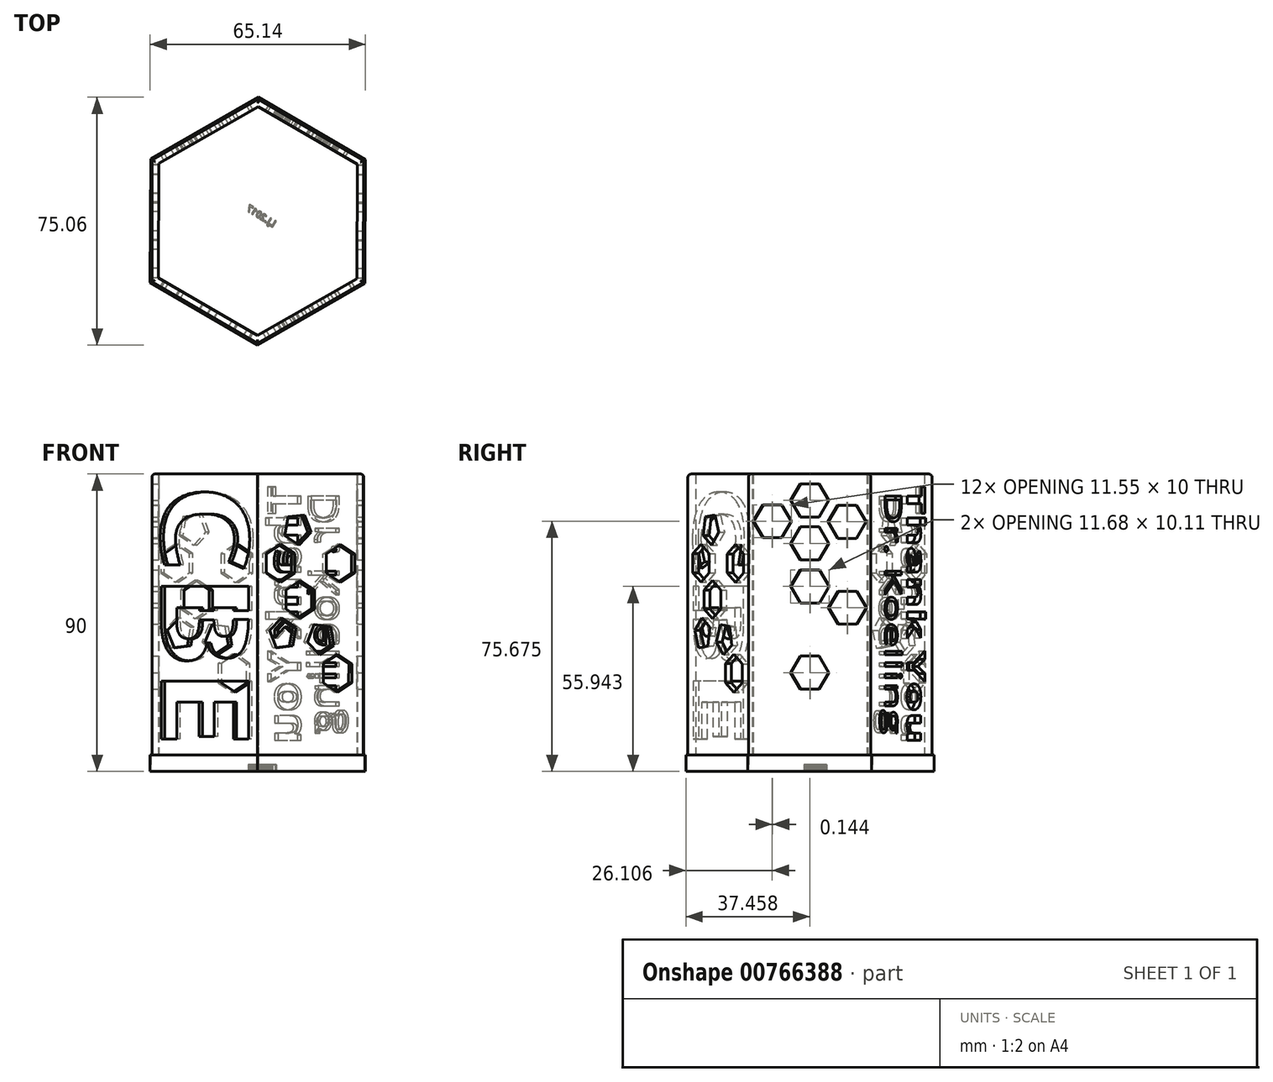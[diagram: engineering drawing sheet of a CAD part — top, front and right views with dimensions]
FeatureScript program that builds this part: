
annotation { "Feature Type Name" : "Feature", "Feature Type Description" : "" }
export const myFeature = defineFeature(function(context is Context, id is Id, definition is map)
    precondition{}
    {
        {
            var Q0;
            Q0=qCreatedBy(makeId("Top.planeOp"),FACE);
            var sketch = newSketch(context, id + "F0", { "sketchPlane" : qUnion([Q0])});
            skCircle(sketch, "E0.cCircle", {"center": v(0, 0) * mm, "radius": 32 * mm, "construction": true});
            skLineSegment(sketch, "E0.0", {"start": v(-31.96, 18.55) * mm, "end": v(0.09, 36.95) * mm});
            skLineSegment(sketch, "E0.1", {"start": v(0.09, 36.95) * mm, "end": v(32.04, 18.4) * mm});
            skLineSegment(sketch, "E0.2", {"start": v(32.04, 18.4) * mm, "end": v(31.96, -18.55) * mm});
            skLineSegment(sketch, "E0.3", {"start": v(31.96, -18.55) * mm, "end": v(-0.09, -36.95) * mm});
            skLineSegment(sketch, "E0.4", {"start": v(-0.09, -36.95) * mm, "end": v(-32.04, -18.4) * mm});
            skLineSegment(sketch, "E0.5", {"start": v(-32.04, -18.4) * mm, "end": v(-31.96, 18.55) * mm});
            skPoint(sketch, "E0.0.midPoint", {"position": v(-15.93, 27.75) * mm});
            skCircle(sketch, "E1.cCircle", {"center": v(0, 0) * mm, "radius": 30 * mm, "construction": true});
            skLineSegment(sketch, "E1.0", {"start": v(-29.93, 17.44) * mm, "end": v(0.13, 34.64) * mm});
            skLineSegment(sketch, "E1.1", {"start": v(0.13, 34.64) * mm, "end": v(30.07, 17.2) * mm});
            skLineSegment(sketch, "E1.2", {"start": v(30.07, 17.2) * mm, "end": v(29.93, -17.44) * mm});
            skLineSegment(sketch, "E1.3", {"start": v(29.93, -17.44) * mm, "end": v(-0.13, -34.64) * mm});
            skLineSegment(sketch, "E1.4", {"start": v(-0.13, -34.64) * mm, "end": v(-30.07, -17.2) * mm});
            skLineSegment(sketch, "E1.5", {"start": v(-30.07, -17.2) * mm, "end": v(-29.93, 17.44) * mm});
            skPoint(sketch, "E1.0.midPoint", {"position": v(-14.9, 26.04) * mm});
            skSolve(sketch);
        }
        {
            var Q0;
            Q0=makeQuery(id+"F0.imprint","IMPRINT",FACE,{"disambiguationData":[TD([[makeQuery(id+"F0.imprint","IMPRINT",EDGE,{"derivedFrom":sQuery(id+"F0.wireOp",EDGE,"E0.0")}),-1.0]])]});
            extrude(context, id + "F1", {"entities" : qUnion([Q0]), "depth" : 90 * mm, "offsetDistance" : 25 * mm});
        }
        {
            var Q0;
            Q0=qCreatedBy(makeId("Top.planeOp"),FACE);
            var sketch = newSketch(context, id + "F2", { "sketchPlane" : qUnion([Q0])});
            skCircle(sketch, "E2.cCircle", {"center": v(0, 0) * mm, "radius": 32.5 * mm, "construction": true});
            skLineSegment(sketch, "E2.0", {"start": v(0.14, 37.53) * mm, "end": v(32.57, 18.64) * mm});
            skLineSegment(sketch, "E2.1", {"start": v(32.57, 18.64) * mm, "end": v(32.43, -18.89) * mm});
            skLineSegment(sketch, "E2.2", {"start": v(32.43, -18.89) * mm, "end": v(-0.14, -37.53) * mm});
            skLineSegment(sketch, "E2.3", {"start": v(-0.14, -37.53) * mm, "end": v(-32.57, -18.64) * mm});
            skLineSegment(sketch, "E2.4", {"start": v(-32.57, -18.64) * mm, "end": v(-32.43, 18.89) * mm});
            skLineSegment(sketch, "E2.5", {"start": v(-32.43, 18.89) * mm, "end": v(0.14, 37.53) * mm});
            skPoint(sketch, "E2.0.midPoint", {"position": v(16.36, 28.08) * mm});
            skSolve(sketch);
        }
        {
            var Q0;
            Q0=makeQuery(id+"F2.imprint","IMPRINT",FACE,{"disambiguationData":[TD([[makeQuery(id+"F2.imprint","IMPRINT",EDGE,{"derivedFrom":sQuery(id+"F2.wireOp",EDGE,"E2.0")}),-1.0]])]});
            extrude(context, id + "F3", {"entities" : qUnion([Q0]), "operationType" : NewBodyOperationType.ADD, "depth" : 5 * mm, "offsetDistance" : 25 * mm});
        }
        {
            var Q0;
            Q0=makeQuery(id+"F1.opExtrude","SWEPT_FACE",FACE,{"disambiguationData":[OSD([sQuery(id+"F0.wireOp",EDGE,"E0.2")])]});
            var sketch = newSketch(context, id + "F4", { "sketchPlane" : qUnion([Q0])});
            skCircle(sketch, "E3.cCircle", {"center": v(0, 82) * mm, "radius": 5 * mm, "construction": true});
            skLineSegment(sketch, "E3.0", {"start": v(-2.89, 87) * mm, "end": v(2.89, 87) * mm});
            skLineSegment(sketch, "E3.1", {"start": v(2.89, 87) * mm, "end": v(5.77, 82) * mm});
            skLineSegment(sketch, "E3.2", {"start": v(5.77, 82) * mm, "end": v(2.89, 77) * mm});
            skLineSegment(sketch, "E3.3", {"start": v(2.89, 77) * mm, "end": v(-2.89, 77) * mm});
            skLineSegment(sketch, "E3.4", {"start": v(-2.89, 77) * mm, "end": v(-5.77, 82) * mm});
            skLineSegment(sketch, "E3.5", {"start": v(-5.77, 82) * mm, "end": v(-2.89, 87) * mm});
            skPoint(sketch, "E3.0.midPoint", {"position": v(0, 87) * mm});
            skCircle(sketch, "E4.cCircle", {"center": v(-11.35, 75.68) * mm, "radius": 5 * mm, "construction": true});
            skLineSegment(sketch, "E4.0", {"start": v(-14.24, 80.68) * mm, "end": v(-8.47, 80.68) * mm});
            skLineSegment(sketch, "E4.1", {"start": v(-8.47, 80.68) * mm, "end": v(-5.58, 75.68) * mm});
            skLineSegment(sketch, "E4.2", {"start": v(-5.58, 75.68) * mm, "end": v(-8.47, 70.68) * mm});
            skLineSegment(sketch, "E4.3", {"start": v(-8.47, 70.68) * mm, "end": v(-14.24, 70.68) * mm});
            skLineSegment(sketch, "E4.4", {"start": v(-14.24, 70.68) * mm, "end": v(-17.13, 75.68) * mm});
            skLineSegment(sketch, "E4.5", {"start": v(-17.13, 75.68) * mm, "end": v(-14.24, 80.68) * mm});
            skPoint(sketch, "E4.0.midPoint", {"position": v(-11.35, 80.68) * mm});
            skCircle(sketch, "E5.cCircle", {"center": v(11.26, 75.5) * mm, "radius": 5 * mm, "construction": true});
            skLineSegment(sketch, "E5.0", {"start": v(8.37, 80.5) * mm, "end": v(14.15, 80.5) * mm});
            skLineSegment(sketch, "E5.1", {"start": v(14.15, 80.5) * mm, "end": v(17.03, 75.5) * mm});
            skLineSegment(sketch, "E5.2", {"start": v(17.03, 75.5) * mm, "end": v(14.15, 70.5) * mm});
            skLineSegment(sketch, "E5.3", {"start": v(14.15, 70.5) * mm, "end": v(8.37, 70.5) * mm});
            skLineSegment(sketch, "E5.4", {"start": v(8.37, 70.5) * mm, "end": v(5.48, 75.5) * mm});
            skLineSegment(sketch, "E5.5", {"start": v(5.48, 75.5) * mm, "end": v(8.37, 80.5) * mm});
            skPoint(sketch, "E5.0.midPoint", {"position": v(11.26, 80.5) * mm});
            skCircle(sketch, "E6.cCircle", {"center": v(0, 69) * mm, "radius": 5 * mm, "construction": true});
            skLineSegment(sketch, "E6.0", {"start": v(-2.89, 74) * mm, "end": v(2.89, 74) * mm});
            skLineSegment(sketch, "E6.1", {"start": v(2.89, 74) * mm, "end": v(5.77, 69) * mm});
            skLineSegment(sketch, "E6.2", {"start": v(5.77, 69) * mm, "end": v(2.89, 64) * mm});
            skLineSegment(sketch, "E6.3", {"start": v(2.89, 64) * mm, "end": v(-2.89, 64) * mm});
            skLineSegment(sketch, "E6.4", {"start": v(-2.89, 64) * mm, "end": v(-5.77, 69) * mm});
            skLineSegment(sketch, "E6.5", {"start": v(-5.77, 69) * mm, "end": v(-2.89, 74) * mm});
            skPoint(sketch, "E6.0.midPoint", {"position": v(0, 74) * mm});
            skCircle(sketch, "E7.cCircle", {"center": v(0, 55.94) * mm, "radius": 5.06 * mm, "construction": true});
            skLineSegment(sketch, "E7.0", {"start": v(-5.84, 55.94) * mm, "end": v(-2.92, 61) * mm});
            skLineSegment(sketch, "E7.1", {"start": v(-2.92, 61) * mm, "end": v(2.92, 61) * mm});
            skLineSegment(sketch, "E7.2", {"start": v(2.92, 61) * mm, "end": v(5.84, 55.94) * mm});
            skLineSegment(sketch, "E7.3", {"start": v(5.84, 55.94) * mm, "end": v(2.92, 50.89) * mm});
            skLineSegment(sketch, "E7.4", {"start": v(2.92, 50.89) * mm, "end": v(-2.92, 50.89) * mm});
            skLineSegment(sketch, "E7.5", {"start": v(-2.92, 50.89) * mm, "end": v(-5.84, 55.94) * mm});
            skPoint(sketch, "E7.0.midPoint", {"position": v(-4.38, 58.47) * mm});
            skCircle(sketch, "E8.cCircle", {"center": v(11.37, 49.53) * mm, "radius": 5 * mm, "construction": true});
            skLineSegment(sketch, "E8.0", {"start": v(5.6, 49.53) * mm, "end": v(8.49, 54.53) * mm});
            skLineSegment(sketch, "E8.1", {"start": v(8.49, 54.53) * mm, "end": v(14.26, 54.53) * mm});
            skLineSegment(sketch, "E8.2", {"start": v(14.26, 54.53) * mm, "end": v(17.15, 49.53) * mm});
            skLineSegment(sketch, "E8.3", {"start": v(17.15, 49.53) * mm, "end": v(14.26, 44.53) * mm});
            skLineSegment(sketch, "E8.4", {"start": v(14.26, 44.53) * mm, "end": v(8.49, 44.53) * mm});
            skLineSegment(sketch, "E8.5", {"start": v(8.49, 44.53) * mm, "end": v(5.6, 49.53) * mm});
            skPoint(sketch, "E8.0.midPoint", {"position": v(7.04, 52.03) * mm});
            skCircle(sketch, "E9.cCircle", {"center": v(0, 29.89) * mm, "radius": 5 * mm, "construction": true});
            skLineSegment(sketch, "E9.0", {"start": v(-5.77, 29.89) * mm, "end": v(-2.89, 34.89) * mm});
            skLineSegment(sketch, "E9.1", {"start": v(-2.89, 34.89) * mm, "end": v(2.89, 34.89) * mm});
            skLineSegment(sketch, "E9.2", {"start": v(2.89, 34.89) * mm, "end": v(5.77, 29.89) * mm});
            skLineSegment(sketch, "E9.3", {"start": v(5.77, 29.89) * mm, "end": v(2.89, 24.89) * mm});
            skLineSegment(sketch, "E9.4", {"start": v(2.89, 24.89) * mm, "end": v(-2.89, 24.89) * mm});
            skLineSegment(sketch, "E9.5", {"start": v(-2.89, 24.89) * mm, "end": v(-5.77, 29.89) * mm});
            skPoint(sketch, "E9.0.midPoint", {"position": v(-4.33, 32.39) * mm});
            skSolve(sketch);
        }
        {
            var Q0;
            Q0=makeQuery(id+"F4.imprint","IMPRINT",FACE,{"disambiguationData":[TD([[makeQuery(id+"F4.imprint","IMPRINT",EDGE,{"derivedFrom":sQuery(id+"F4.wireOp",EDGE,"E3.0")}),-1.0]])]});
            var Q1;
            Q1=makeQuery(id+"F4.imprint","IMPRINT",FACE,{"disambiguationData":[TD([[makeQuery(id+"F4.imprint","IMPRINT",EDGE,{"derivedFrom":sQuery(id+"F4.wireOp",EDGE,"E5.0")}),-1.0]])]});
            var Q2;
            Q2=makeQuery(id+"F4.imprint","IMPRINT",FACE,{"disambiguationData":[TD([[makeQuery(id+"F4.imprint","IMPRINT",EDGE,{"derivedFrom":sQuery(id+"F4.wireOp",EDGE,"E4.0")}),-1.0]])]});
            var Q3;
            Q3=makeQuery(id+"F4.imprint","IMPRINT",FACE,{"disambiguationData":[TD([[makeQuery(id+"F4.imprint","IMPRINT",EDGE,{"derivedFrom":sQuery(id+"F4.wireOp",EDGE,"E6.0")}),-1.0]])]});
            var Q4;
            Q4=makeQuery(id+"F4.imprint","IMPRINT",FACE,{"disambiguationData":[TD([[makeQuery(id+"F4.imprint","IMPRINT",EDGE,{"derivedFrom":sQuery(id+"F4.wireOp",EDGE,"E7.0")}),-1.0]])]});
            var Q5;
            Q5=makeQuery(id+"F4.imprint","IMPRINT",FACE,{"disambiguationData":[TD([[makeQuery(id+"F4.imprint","IMPRINT",EDGE,{"derivedFrom":sQuery(id+"F4.wireOp",EDGE,"E8.0")}),-1.0]])]});
            var Q6;
            Q6=makeQuery(id+"F4.imprint","IMPRINT",FACE,{"disambiguationData":[TD([[makeQuery(id+"F4.imprint","IMPRINT",EDGE,{"derivedFrom":sQuery(id+"F4.wireOp",EDGE,"E9.0")}),-1.0]])]});
            extrude(context, id + "F5", {"entities" : qUnion([Q0, Q1, Q2, Q3, Q4, Q5, Q6]), "operationType" : NewBodyOperationType.REMOVE, "oppositeDirection" : true, "depth" : 100 * mm, "offsetDistance" : 25 * mm});
        }
        {
            var Q0;
            Q0=makeQuery(id+"F1.opExtrude","CAP_EDGE",EDGE,{"disambiguationData":[OSD([sQuery(id+"F0.wireOp",EDGE,"E0.0")])],"isStart":false});
            var Q1;
            Q1=makeQuery(id+"F1.opExtrude","CAP_EDGE",EDGE,{"disambiguationData":[OSD([sQuery(id+"F0.wireOp",EDGE,"E0.5")])],"isStart":false});
            var Q2;
            Q2=makeQuery(id+"F1.opExtrude","CAP_EDGE",EDGE,{"disambiguationData":[OSD([sQuery(id+"F0.wireOp",EDGE,"E0.2")])],"isStart":false});
            var Q3;
            Q3=makeQuery(id+"F1.opExtrude","CAP_EDGE",EDGE,{"disambiguationData":[OSD([sQuery(id+"F0.wireOp",EDGE,"E0.3")])],"isStart":false});
            var Q4;
            Q4=makeQuery(id+"F1.opExtrude","CAP_EDGE",EDGE,{"disambiguationData":[OSD([sQuery(id+"F0.wireOp",EDGE,"E0.4")])],"isStart":false});
            var Q5;
            Q5=makeQuery(id+"F1.opExtrude","CAP_EDGE",EDGE,{"disambiguationData":[OSD([sQuery(id+"F0.wireOp",EDGE,"E0.1")])],"isStart":false});
            fillet(context, id + "F6", {"entities" : qUnion([Q0, Q1, Q2, Q3, Q4, Q5]), "radius" : 1 * mm, "tangentPropagation" : true, "allowEdgeOverflow" : false});
        }
        {
            var Q0;
            Q0=makeQuery(id+"F1.opExtrude","SWEPT_FACE",FACE,{"disambiguationData":[OSD([sQuery(id+"F0.wireOp",EDGE,"E0.0")])]});
            var sketch = newSketch(context, id + "F7", { "sketchPlane" : qUnion([Q0])});
            skCircle(sketch, "E10.cCircle", {"center": v(-10.48, 62.93) * mm, "radius": 5 * mm, "construction": true});
            skLineSegment(sketch, "E10.0", {"start": v(-15.48, 65.82) * mm, "end": v(-10.48, 68.7) * mm});
            skLineSegment(sketch, "E10.1", {"start": v(-10.48, 68.7) * mm, "end": v(-5.48, 65.82) * mm});
            skLineSegment(sketch, "E10.2", {"start": v(-5.48, 65.82) * mm, "end": v(-5.48, 60.04) * mm});
            skLineSegment(sketch, "E10.3", {"start": v(-5.48, 60.04) * mm, "end": v(-10.48, 57.16) * mm});
            skLineSegment(sketch, "E10.4", {"start": v(-10.48, 57.16) * mm, "end": v(-15.48, 60.04) * mm});
            skLineSegment(sketch, "E10.5", {"start": v(-15.48, 60.04) * mm, "end": v(-15.48, 65.82) * mm});
            skPoint(sketch, "E10.0.midPoint", {"position": v(-12.98, 67.26) * mm});
            skCircle(sketch, "E11.cCircle", {"center": v(10.48, 62.98) * mm, "radius": 5 * mm, "construction": true});
            skLineSegment(sketch, "E11.0", {"start": v(5.48, 65.87) * mm, "end": v(10.48, 68.75) * mm});
            skLineSegment(sketch, "E11.1", {"start": v(10.48, 68.75) * mm, "end": v(15.48, 65.87) * mm});
            skLineSegment(sketch, "E11.2", {"start": v(15.48, 65.87) * mm, "end": v(15.48, 60.1) * mm});
            skLineSegment(sketch, "E11.3", {"start": v(15.48, 60.1) * mm, "end": v(10.48, 57.2) * mm});
            skLineSegment(sketch, "E11.4", {"start": v(10.48, 57.2) * mm, "end": v(5.48, 60.1) * mm});
            skLineSegment(sketch, "E11.5", {"start": v(5.48, 60.1) * mm, "end": v(5.48, 65.87) * mm});
            skPoint(sketch, "E11.0.midPoint", {"position": v(7.98, 67.3) * mm});
            skCircle(sketch, "E12.cCircle", {"center": v(3.52, 51.98) * mm, "radius": 5 * mm, "construction": true});
            skLineSegment(sketch, "E12.0", {"start": v(-1.48, 54.87) * mm, "end": v(3.52, 57.75) * mm});
            skLineSegment(sketch, "E12.1", {"start": v(3.52, 57.75) * mm, "end": v(8.52, 54.87) * mm});
            skLineSegment(sketch, "E12.2", {"start": v(8.52, 54.87) * mm, "end": v(8.52, 49.1) * mm});
            skLineSegment(sketch, "E12.3", {"start": v(8.52, 49.1) * mm, "end": v(3.52, 46.2) * mm});
            skLineSegment(sketch, "E12.4", {"start": v(3.52, 46.2) * mm, "end": v(-1.48, 49.1) * mm});
            skLineSegment(sketch, "E12.5", {"start": v(-1.48, 49.1) * mm, "end": v(-1.48, 54.87) * mm});
            skPoint(sketch, "E12.0.midPoint", {"position": v(1.02, 56.31) * mm});
            skCircle(sketch, "E13.cCircle", {"center": v(-9.5, 29.7) * mm, "radius": 5 * mm, "construction": true});
            skLineSegment(sketch, "E13.0", {"start": v(-14.5, 32.56) * mm, "end": v(-9.52, 35.47) * mm});
            skLineSegment(sketch, "E13.1", {"start": v(-9.52, 35.47) * mm, "end": v(-4.5, 32.61) * mm});
            skLineSegment(sketch, "E13.2", {"start": v(-4.5, 32.61) * mm, "end": v(-4.48, 26.84) * mm});
            skLineSegment(sketch, "E13.3", {"start": v(-4.48, 26.84) * mm, "end": v(-9.46, 23.92) * mm});
            skLineSegment(sketch, "E13.4", {"start": v(-9.46, 23.92) * mm, "end": v(-14.48, 26.79) * mm});
            skLineSegment(sketch, "E13.5", {"start": v(-14.48, 26.79) * mm, "end": v(-14.5, 32.56) * mm});
            skPoint(sketch, "E13.0.midPoint", {"position": v(-12.01, 34.01) * mm});
            skCircle(sketch, "E14.cCircle", {"center": v(9.5, 41.6) * mm, "radius": 3.97 * mm, "construction": true});
            skLineSegment(sketch, "E14.0", {"start": v(10.02, 46.5) * mm, "end": v(14.3, 42.63) * mm});
            skLineSegment(sketch, "E14.1", {"start": v(14.3, 42.63) * mm, "end": v(11.96, 37.36) * mm});
            skLineSegment(sketch, "E14.2", {"start": v(11.96, 37.36) * mm, "end": v(6.22, 37.96) * mm});
            skLineSegment(sketch, "E14.3", {"start": v(6.22, 37.96) * mm, "end": v(5.02, 43.6) * mm});
            skLineSegment(sketch, "E14.4", {"start": v(5.02, 43.6) * mm, "end": v(10.02, 46.5) * mm});
            skPoint(sketch, "E14.0.midPoint", {"position": v(12.16, 44.56) * mm});
            skCircle(sketch, "E15.cCircle", {"center": v(-3.67, 40.16) * mm, "radius": 3.97 * mm, "construction": true});
            skLineSegment(sketch, "E15.0", {"start": v(1.14, 39.16) * mm, "end": v(-3.13, 35.28) * mm});
            skLineSegment(sketch, "E15.1", {"start": v(-3.13, 35.28) * mm, "end": v(-8.14, 38.14) * mm});
            skLineSegment(sketch, "E15.2", {"start": v(-8.14, 38.14) * mm, "end": v(-6.97, 43.8) * mm});
            skLineSegment(sketch, "E15.3", {"start": v(-6.97, 43.8) * mm, "end": v(-1.24, 44.43) * mm});
            skLineSegment(sketch, "E15.4", {"start": v(-1.24, 44.43) * mm, "end": v(1.14, 39.16) * mm});
            skPoint(sketch, "E15.0.midPoint", {"position": v(-1, 37.22) * mm});
            skCircle(sketch, "E16.cCircle", {"center": v(4.52, 73.36) * mm, "radius": 3.97 * mm, "construction": true});
            skLineSegment(sketch, "E16.0", {"start": v(-0.29, 72.34) * mm, "end": v(2.06, 77.62) * mm});
            skLineSegment(sketch, "E16.1", {"start": v(2.06, 77.62) * mm, "end": v(7.8, 77.01) * mm});
            skLineSegment(sketch, "E16.2", {"start": v(7.8, 77.01) * mm, "end": v(9, 71.37) * mm});
            skLineSegment(sketch, "E16.3", {"start": v(9, 71.37) * mm, "end": v(4, 68.48) * mm});
            skLineSegment(sketch, "E16.4", {"start": v(4, 68.48) * mm, "end": v(-0.29, 72.34) * mm});
            skPoint(sketch, "E16.0.midPoint", {"position": v(0.89, 74.98) * mm});
            skSolve(sketch);
        }
        {
            var Q0;
            Q0 = qSketchRegion(id + "F7", true);
            extrude(context, id + "F8", {"entities" : qUnion([Q0]), "operationType" : NewBodyOperationType.REMOVE, "oppositeDirection" : true, "depth" : 100 * mm, "offsetDistance" : 25 * mm});
        }
        {
            var Q0;
            Q0=makeQuery(id+"F1.opExtrude","SWEPT_FACE",FACE,{"disambiguationData":[OSD([sQuery(id+"F0.wireOp",EDGE,"E0.4")])]});
            var sketch = newSketch(context, id + "F9", { "sketchPlane" : qUnion([Q0])});
            skText(sketch, "E17", { "text": "CBE", "fontName": "OpenSans-Bold.ttf"});
            skLineSegment(sketch, "E18", {"start": v(9.93, 48.67) * mm, "end": v(15.57, 48.67) * mm});
            skLineSegment(sketch, "E19", {"start": v(9.93, 45.9) * mm, "end": v(15.57, 45.9) * mm});
            skLineSegment(sketch, "E20", {"start": v(-15.15, 48.67) * mm, "end": v(-9.77, 48.67) * mm});
            skLineSegment(sketch, "E21", {"start": v(-15.15, 45.9) * mm, "end": v(-9.77, 45.9) * mm});
            skLineSegment(sketch, "E22", {"start": v(-1.88, 48.67) * mm, "end": v(3.3, 48.67) * mm});
            skLineSegment(sketch, "E23", {"start": v(3.3, 45.8) * mm, "end": v(-1.88, 45.8) * mm});
            const initialGuessF9  = {"E17": [-0.01515, 0.08703, 0, -1, 0.03072]};
            skSetInitialGuess(sketch, initialGuessF9);
            skSolve(sketch);
        }
        {
            var Q0;
            Q0=makeQuery(id+"F9.imprint","IMPRINT",FACE,{"disambiguationData":[TD([[makeQuery(id+"F9.imprint","IMPRINT",EDGE,{"derivedFrom":sQuery(id+"F9.wireOp",EDGE,"E17.sketch_text.stroke-0")}),-1.0]])]});
            var Q1;
            {var subQ6=sQuery(id+"F9.wireOp",EDGE,"E17.sketch_text.stroke-26");Q1=makeQuery(id+"F9.imprint","IMPRINT",FACE,{"disambiguationData":[TD([[makeQuery(id+"F9.imprint","IMPRINT",EDGE,{"derivedFrom":subQ6}),-1.0]])]});}
            var Q2;
            {var subQ15=sQuery(id+"F9.wireOp",EDGE,"E17.sketch_text.stroke-17");Q2=makeQuery(id+"F9.imprint","IMPRINT",FACE,{"disambiguationData":[TD([[makeQuery(id+"F9.imprint","IMPRINT",EDGE,{"derivedFrom":subQ15}),-1.0]])]});}
            var Q3;
            Q3=makeQuery(id+"F9.imprint","IMPRINT",FACE,{"disambiguationData":[TD([[makeQuery(id+"F9.imprint","IMPRINT",EDGE,{"derivedFrom":sQuery(id+"F9.wireOp",EDGE,"E17.sketch_text.stroke-40")}),-1.0]])]});
            extrude(context, id + "F10", {"entities" : qUnion([Q0, Q1, Q2, Q3]), "operationType" : NewBodyOperationType.REMOVE, "oppositeDirection" : true, "depth" : 30 * mm, "offsetDistance" : 25 * mm});
        }
        {
            var Q0;
            Q0=makeQuery(id+"F1.opExtrude","SWEPT_FACE",FACE,{"disambiguationData":[OSD([sQuery(id+"F0.wireOp",EDGE,"E0.1")])]});
            var sketch = newSketch(context, id + "F11", { "sketchPlane" : qUnion([Q0])});
            skText(sketch, "E24", { "text": "Thank You", "fontName": "OpenSans-Bold.ttf"});
            const initialGuessF11  = {"E24": [0.00347, 0.08644, 0, -1, 0.01067]};
            skSetInitialGuess(sketch, initialGuessF11);
            skSolve(sketch);
        }
        {
            var Q0;
            Q0=makeQuery(id+"F11.imprint","IMPRINT",FACE,{"disambiguationData":[TD([[makeQuery(id+"F11.imprint","IMPRINT",EDGE,{"derivedFrom":sQuery(id+"F11.wireOp",EDGE,"E24.sketch_text.stroke-0")}),1.0]])]});
            var sketch = newSketch(context, id + "F12", { "sketchPlane" : qUnion([Q0])});
            skText(sketch, "E25", { "text": "Dr. Koelling", "fontName": "OpenSans-Regular.ttf"});
            const initialGuessF12  = {"E25": [-0.00986, 0.08466, 0, -1, 0.00986]};
            skSetInitialGuess(sketch, initialGuessF12);
            skSolve(sketch);
        }
        {
            var Q0;
            Q0 = qSketchRegion(id + "F11", true);
            var Q1;
            Q1 = qSketchRegion(id + "F12", true);
            extrude(context, id + "F13", {"entities" : qUnion([Q0, Q1]), "operationType" : NewBodyOperationType.REMOVE, "oppositeDirection" : true, "depth" : 25 * mm, "offsetDistance" : 25 * mm});
        }
        {
            var Q0;
            Q0=makeQuery(id+"F3.boolean.opBoolean","MERGE",FACE,{"derivedFrom":[makeQuery(id+"F1.opExtrude","CAP_FACE",FACE,{"disambiguationData":[OSD([sQuery(id+"F0.wireOp",EDGE,"E0.0"),sQuery(id+"F0.wireOp",EDGE,"E0.1"),sQuery(id+"F0.wireOp",EDGE,"E0.2"),sQuery(id+"F0.wireOp",EDGE,"E0.3"),sQuery(id+"F0.wireOp",EDGE,"E0.4"),sQuery(id+"F0.wireOp",EDGE,"E0.5"),sQuery(id+"F0.wireOp",EDGE,"E1.0"),sQuery(id+"F0.wireOp",EDGE,"E1.1"),sQuery(id+"F0.wireOp",EDGE,"E1.2"),sQuery(id+"F0.wireOp",EDGE,"E1.3"),sQuery(id+"F0.wireOp",EDGE,"E1.4"),sQuery(id+"F0.wireOp",EDGE,"E1.5")])],"isStart":true}),makeQuery(id+"F3.opExtrude","CAP_FACE",FACE,{"disambiguationData":[OSD([sQuery(id+"F2.wireOp",EDGE,"E2.0"),sQuery(id+"F2.wireOp",EDGE,"E2.1"),sQuery(id+"F2.wireOp",EDGE,"E2.2"),sQuery(id+"F2.wireOp",EDGE,"E2.3"),sQuery(id+"F2.wireOp",EDGE,"E2.4"),sQuery(id+"F2.wireOp",EDGE,"E2.5")])],"isStart":true})]});
            var sketch = newSketch(context, id + "F14", { "sketchPlane" : qUnion([Q0])});
            skText(sketch, "E26", { "text": "LJ.2017", "fontName": "OpenSans-Bold.ttf"});
            const initialGuessF14  = {"E26": [0.00473, 0.00193, -0.84805, -0.52992, 0.00206]};
            skSetInitialGuess(sketch, initialGuessF14);
            skSolve(sketch);
        }
        {
            var Q0;
            Q0 = qSketchRegion(id + "F14", true);
            extrude(context, id + "F15", {"entities" : qUnion([Q0]), "operationType" : NewBodyOperationType.REMOVE, "oppositeDirection" : true, "depth" : 2 * mm, "offsetDistance" : 25 * mm});
        }
    });
